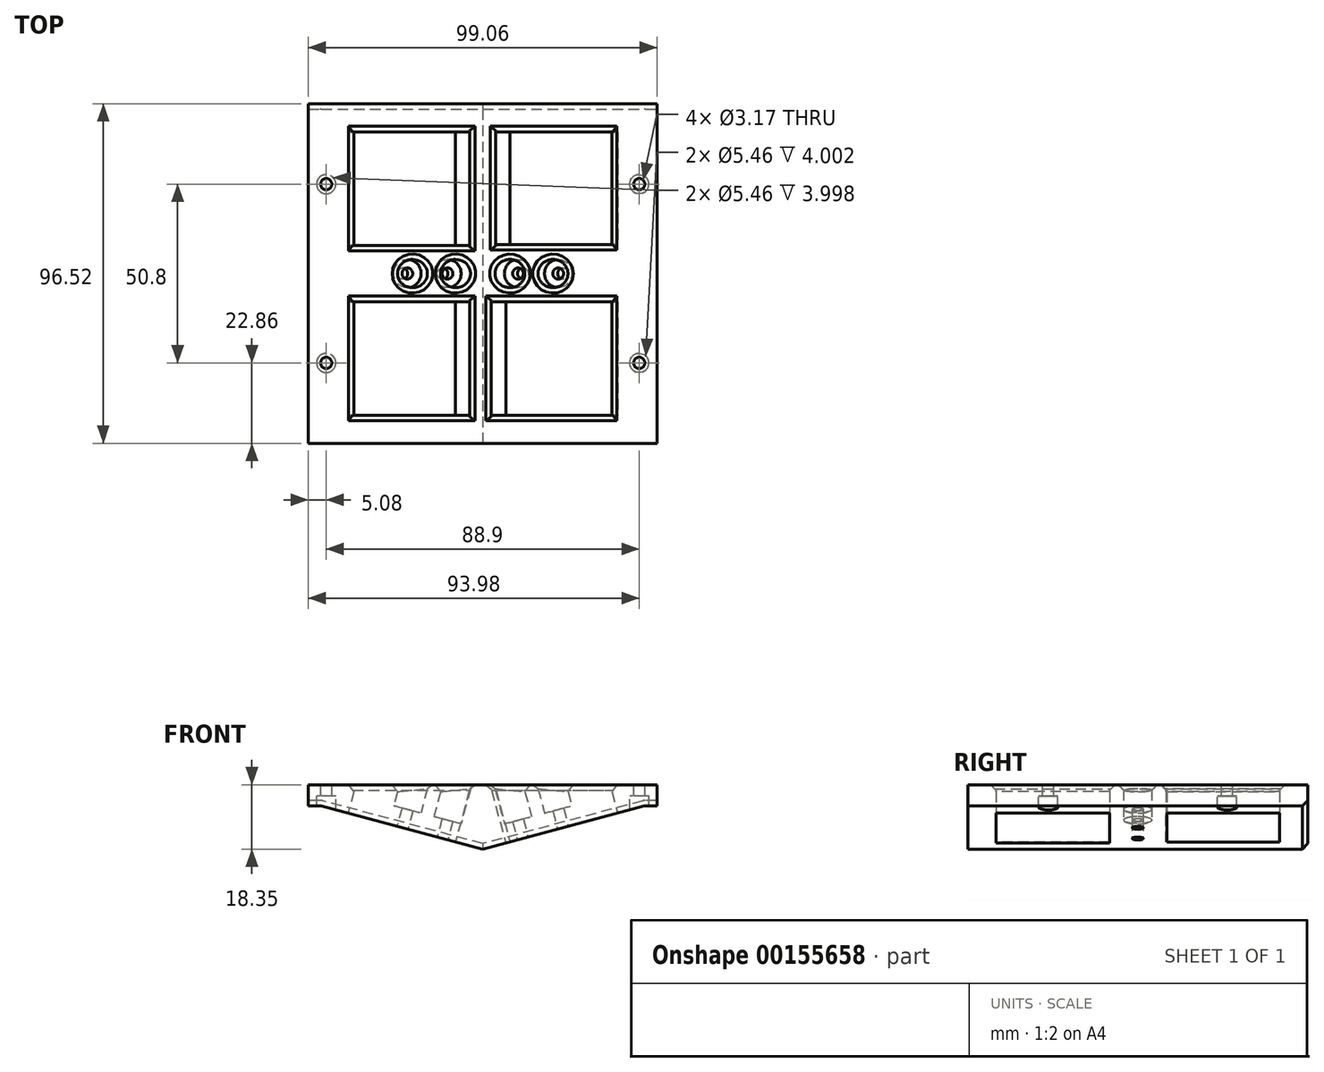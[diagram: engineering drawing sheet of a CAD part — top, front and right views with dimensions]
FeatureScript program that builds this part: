
annotation { "Feature Type Name" : "Feature", "Feature Type Description" : "" }
export const myFeature = defineFeature(function(context is Context, id is Id, definition is map)
    precondition{}
    {
        {
            var Q0;
            Q0=qCreatedBy(makeId("Top.planeOp"),FACE);
            var sketch = newSketch(context, id + "F0", { "sketchPlane" : qUnion([Q0])});
            skLineSegment(sketch, "E0", {"start": v(0, 0) * mm, "end": v(0, 48.26) * mm});
            skLineSegment(sketch, "E1", {"start": v(0, 48.26) * mm, "end": v(-49.53, 48.26) * mm});
            skLineSegment(sketch, "E2", {"start": v(-49.53, 48.26) * mm, "end": v(-49.53, 0) * mm});
            skLineSegment(sketch, "E3", {"start": v(-49.53, 0) * mm, "end": v(0, 0) * mm});
            skLineSegment(sketch, "E4", {"start": v(-49.53, 0) * mm, "end": v(-49.53, -48.26) * mm});
            skLineSegment(sketch, "E5", {"start": v(-49.53, -48.26) * mm, "end": v(0, -48.26) * mm});
            skLineSegment(sketch, "E6", {"start": v(0, -48.26) * mm, "end": v(0, 0) * mm});
            skLineSegment(sketch, "E7.MirrorCS", {"start": v(0, 48.26) * mm, "end": v(49.53, 48.26) * mm});
            skLineSegment(sketch, "E8.MirrorCS", {"start": v(49.53, 48.26) * mm, "end": v(49.53, 0) * mm});
            skLineSegment(sketch, "E9.MirrorCS", {"start": v(49.53, 0) * mm, "end": v(0, 0) * mm});
            skLineSegment(sketch, "E10.MirrorCS", {"start": v(49.53, -48.26) * mm, "end": v(0, -48.26) * mm});
            skLineSegment(sketch, "E11.MirrorCS", {"start": v(49.53, 0) * mm, "end": v(49.53, -48.26) * mm});
            skSolve(sketch);
        }
        {
            var Q0;
            Q0 = qSketchRegion(id + "F0", true);
            extrude(context, id + "F1", {"entities" : qUnion([Q0]), "depth" : 18.35 * mm});
        }
        {
            var Q0;
            Q0=makeQuery(id+"F1.opExtrude","SWEPT_FACE",FACE,{"disambiguationData":[OSD([sQuery(id+"F0.wireOp",EDGE,"E5"),sQuery(id+"F0.wireOp",EDGE,"E10.MirrorCS")])]});
            var sketch = newSketch(context, id + "F2", { "sketchPlane" : qUnion([Q0])});
            skLineSegment(sketch, "E12", {"start": v(0, 0) * mm, "end": v(-46, 12.33) * mm});
            skLineSegment(sketch, "E13", {"start": v(-46, 12.33) * mm, "end": v(-49.53, 12.33) * mm});
            skLineSegment(sketch, "E14", {"start": v(-49.53, 12.33) * mm, "end": v(-49.53, 0) * mm});
            skLineSegment(sketch, "E15", {"start": v(-49.53, 0) * mm, "end": v(0, 0) * mm});
            skLineSegment(sketch, "E16.MirrorCS", {"start": v(0, 0) * mm, "end": v(46, 12.33) * mm});
            skLineSegment(sketch, "E17.MirrorCS", {"start": v(49.53, 12.33) * mm, "end": v(49.53, 0) * mm});
            skLineSegment(sketch, "E18.MirrorCS", {"start": v(49.53, 0) * mm, "end": v(0, 0) * mm});
            skLineSegment(sketch, "E19.MirrorCS", {"start": v(46, 12.33) * mm, "end": v(49.53, 12.33) * mm});
            skSolve(sketch);
        }
        {
            var Q0;
            Q0 = qSketchRegion(id + "F2", true);
            extrude(context, id + "F3", {"entities" : qUnion([Q0]), "operationType" : NewBodyOperationType.REMOVE, "oppositeDirection" : true, "depth" : 101.6 * mm});
        }
        {
            var Q0;
            Q0=makeQuery(id+"F3.boolean.opBoolean","COPY",FACE,{"derivedFrom":makeQuery(id+"F3.opExtrude","SWEPT_FACE",FACE,{"disambiguationData":[OSD([sQuery(id+"F2.wireOp",EDGE,"E12")])]})});
            var sketch = newSketch(context, id + "F4", { "sketchPlane" : qUnion([Q0])});
            skCircle(sketch, "E20", {"center": v(-23.62, 0) * mm, "radius": 4 * mm});
            skCircle(sketch, "E21", {"center": v(-11.81, 0) * mm, "radius": 4 * mm});
            skLineSegment(sketch, "E22", {"start": v(-39.62, 40.26) * mm, "end": v(-39.62, 8) * mm});
            skLineSegment(sketch, "E23", {"start": v(-39.62, 8) * mm, "end": v(-8, 8) * mm});
            skLineSegment(sketch, "E24", {"start": v(-8, 8) * mm, "end": v(-8, 40.26) * mm});
            skLineSegment(sketch, "E25", {"start": v(-8, 40.26) * mm, "end": v(-39.62, 40.26) * mm});
            skLineSegment(sketch, "E26", {"start": v(-39.62, -8) * mm, "end": v(-39.62, -40.26) * mm});
            skLineSegment(sketch, "E27", {"start": v(-39.62, -40.26) * mm, "end": v(-8, -40.26) * mm});
            skLineSegment(sketch, "E28", {"start": v(-8, -40.26) * mm, "end": v(-8, -8) * mm});
            skLineSegment(sketch, "E29", {"start": v(-8, -8) * mm, "end": v(-39.62, -8) * mm});
            skSolve(sketch);
        }
        {
            var Q0;
            Q0 = qSketchRegion(id + "F4", true);
            extrude(context, id + "F5", {"entities" : qUnion([Q0]), "operationType" : NewBodyOperationType.REMOVE, "oppositeDirection" : true, "depth" : 25.4 * mm});
        }
        {
            var Q0;
            Q0=makeQuery(id+"F3.boolean.opBoolean","COPY",FACE,{"derivedFrom":makeQuery(id+"F3.opExtrude","SWEPT_FACE",FACE,{"disambiguationData":[OSD([sQuery(id+"F2.wireOp",EDGE,"E16.MirrorCS")])]})});
            var sketch = newSketch(context, id + "F6", { "sketchPlane" : qUnion([Q0])});
            skCircle(sketch, "E30", {"center": v(23.62, 0) * mm, "radius": 4 * mm});
            skCircle(sketch, "E31", {"center": v(11.81, 0) * mm, "radius": 4 * mm});
            skLineSegment(sketch, "E32", {"start": v(6.77, 40.26) * mm, "end": v(6.77, 8) * mm});
            skLineSegment(sketch, "E33", {"start": v(6.77, 8) * mm, "end": v(39.62, 8) * mm});
            skLineSegment(sketch, "E34", {"start": v(39.62, 8) * mm, "end": v(39.62, 40.26) * mm});
            skLineSegment(sketch, "E35", {"start": v(39.62, 40.26) * mm, "end": v(6.77, 40.26) * mm});
            skLineSegment(sketch, "E36", {"start": v(8, -8.25) * mm, "end": v(8, -40.26) * mm});
            skLineSegment(sketch, "E37", {"start": v(8, -40.26) * mm, "end": v(39.62, -40.26) * mm});
            skLineSegment(sketch, "E38", {"start": v(39.62, -40.26) * mm, "end": v(39.62, -8.25) * mm});
            skLineSegment(sketch, "E39", {"start": v(39.62, -8.25) * mm, "end": v(8, -8.25) * mm});
            skSolve(sketch);
        }
        {
            var Q0;
            Q0 = qSketchRegion(id + "F6", true);
            extrude(context, id + "F7", {"entities" : qUnion([Q0]), "operationType" : NewBodyOperationType.REMOVE, "oppositeDirection" : true, "depth" : 25.4 * mm});
        }
        {
            var Q0;
            Q0=makeQuery(id+"F3.boolean.opBoolean","COPY",FACE,{"derivedFrom":makeQuery(id+"F3.opExtrude","SWEPT_FACE",FACE,{"disambiguationData":[OSD([sQuery(id+"F2.wireOp",EDGE,"E12")])]})});
            var sketch = newSketch(context, id + "F8", { "sketchPlane" : qUnion([Q0])});
            skCircle(sketch, "E40", {"center": v(-23.62, 0) * mm, "radius": 4 * mm});
            skCircle(sketch, "E41", {"center": v(-11.81, 0) * mm, "radius": 4 * mm});
            skSolve(sketch);
        }
        {
            var Q0;
            Q0 = qSketchRegion(id + "F8", true);
            extrude(context, id + "F9", {"entities" : qUnion([Q0]), "operationType" : NewBodyOperationType.ADD, "oppositeDirection" : true, "depth" : 5.46 * mm});
        }
        {
            var Q0;
            Q0=makeQuery(id+"F9.boolean.opBoolean","MERGE",FACE,{"derivedFrom":[makeQuery(id+"F3.boolean.opBoolean","COPY",FACE,{"derivedFrom":makeQuery(id+"F3.opExtrude","SWEPT_FACE",FACE,{"disambiguationData":[OSD([sQuery(id+"F2.wireOp",EDGE,"E12")])]})}),makeQuery(id+"F9.opExtrude","CAP_FACE",FACE,{"disambiguationData":[OSD([sQuery(id+"F8.wireOp",EDGE,"pQ3E8yyw-vJVo-3WWa-J51h-BuG9gktovIe7")])],"isStart":true}),makeQuery(id+"F9.opExtrude","CAP_FACE",FACE,{"disambiguationData":[OSD([sQuery(id+"F8.wireOp",EDGE,"E40")])],"isStart":true}),makeQuery(id+"F9.opExtrude","CAP_FACE",FACE,{"disambiguationData":[OSD([sQuery(id+"F8.wireOp",EDGE,"E41")])],"isStart":true})]});
            var sketch = newSketch(context, id + "F10", { "sketchPlane" : qUnion([Q0])});
            skCircle(sketch, "E42", {"center": v(-11.81, 0) * mm, "radius": 1.59 * mm});
            skCircle(sketch, "E43", {"center": v(-23.62, 0) * mm, "radius": 1.59 * mm});
            skSolve(sketch);
        }
        {
            var Q0;
            Q0 = qSketchRegion(id + "F10", true);
            extrude(context, id + "F11", {"entities" : qUnion([Q0]), "operationType" : NewBodyOperationType.REMOVE, "oppositeDirection" : true, "depth" : 25.4 * mm});
        }
        {
            var Q0;
            Q0=makeQuery(id+"F3.boolean.opBoolean","COPY",FACE,{"derivedFrom":makeQuery(id+"F3.opExtrude","SWEPT_FACE",FACE,{"disambiguationData":[OSD([sQuery(id+"F2.wireOp",EDGE,"E16.MirrorCS")])]})});
            var sketch = newSketch(context, id + "F12", { "sketchPlane" : qUnion([Q0])});
            skCircle(sketch, "E44", {"center": v(11.81, 0) * mm, "radius": 4 * mm});
            skCircle(sketch, "E45", {"center": v(23.62, 0) * mm, "radius": 4 * mm});
            skSolve(sketch);
        }
        {
            var Q0;
            Q0 = qSketchRegion(id + "F12", true);
            extrude(context, id + "F13", {"entities" : qUnion([Q0]), "operationType" : NewBodyOperationType.ADD, "oppositeDirection" : true, "depth" : 5.4 * mm});
        }
        {
            var Q0;
            Q0=makeQuery(id+"F13.boolean.opBoolean","MERGE",FACE,{"derivedFrom":[makeQuery(id+"F3.boolean.opBoolean","COPY",FACE,{"derivedFrom":makeQuery(id+"F3.opExtrude","SWEPT_FACE",FACE,{"disambiguationData":[OSD([sQuery(id+"F2.wireOp",EDGE,"E16.MirrorCS")])]})}),makeQuery(id+"F13.opExtrude","CAP_FACE",FACE,{"disambiguationData":[OSD([sQuery(id+"F12.wireOp",EDGE,"E44")])],"isStart":true}),makeQuery(id+"F13.opExtrude","CAP_FACE",FACE,{"disambiguationData":[OSD([sQuery(id+"F12.wireOp",EDGE,"E45")])],"isStart":true})]});
            var sketch = newSketch(context, id + "F14", { "sketchPlane" : qUnion([Q0])});
            skCircle(sketch, "E46", {"center": v(11.81, 0) * mm, "radius": 1.59 * mm});
            skCircle(sketch, "E47", {"center": v(23.62, 0) * mm, "radius": 1.59 * mm});
            skSolve(sketch);
        }
        {
            var Q0;
            Q0 = qSketchRegion(id + "F14", true);
            extrude(context, id + "F15", {"entities" : qUnion([Q0]), "operationType" : NewBodyOperationType.REMOVE, "oppositeDirection" : true, "depth" : 19.05 * mm});
        }
        {
            var Q0;
            Q0=makeQuery(id+"F3.boolean.opBoolean","COPY",EDGE,{"derivedFrom":makeQuery(id+"F3.opExtrude","SWEPT_EDGE",EDGE,{"disambiguationData":[OSD([sQuery(id+"F2.wireOp",EDGE,"E12"),sQuery(id+"F2.wireOp",EDGE,"E13")])]})});
            var Q1;
            Q1=makeQuery(id+"F3.boolean.opBoolean","COPY",EDGE,{"derivedFrom":makeQuery(id+"F3.opExtrude","SWEPT_EDGE",EDGE,{"disambiguationData":[OSD([sQuery(id+"F2.wireOp",EDGE,"E16.MirrorCS"),sQuery(id+"F2.wireOp",EDGE,"E19.MirrorCS")])]})});
            fillet(context, id + "F16", {"entities" : qUnion([Q0, Q1]), "radius" : 1.59 * mm, "tangentPropagation" : true, "allowEdgeOverflow" : false});
        }
        {
            var Q0;
            Q0=makeQuery(id+"F7.boolean.opBoolean","INTERSECT",EDGE,{"derivedFrom":[makeQuery(id+"F1.opExtrude","CAP_FACE",FACE,{"disambiguationData":[OSD([sQuery(id+"F0.wireOp",EDGE,"E1"),sQuery(id+"F0.wireOp",EDGE,"E2"),sQuery(id+"F0.wireOp",EDGE,"E4"),sQuery(id+"F0.wireOp",EDGE,"E5"),sQuery(id+"F0.wireOp",EDGE,"E7.MirrorCS"),sQuery(id+"F0.wireOp",EDGE,"E8.MirrorCS"),sQuery(id+"F0.wireOp",EDGE,"E10.MirrorCS"),sQuery(id+"F0.wireOp",EDGE,"E11.MirrorCS")])],"isStart":false}),makeQuery(id+"F7.opExtrude","SWEPT_FACE",FACE,{"disambiguationData":[OSD([sQuery(id+"F6.wireOp",EDGE,"E31")])]})]});
            var Q1;
            Q1=makeQuery(id+"F7.boolean.opBoolean","INTERSECT",EDGE,{"derivedFrom":[makeQuery(id+"F1.opExtrude","CAP_FACE",FACE,{"disambiguationData":[OSD([sQuery(id+"F0.wireOp",EDGE,"E1"),sQuery(id+"F0.wireOp",EDGE,"E2"),sQuery(id+"F0.wireOp",EDGE,"E4"),sQuery(id+"F0.wireOp",EDGE,"E5"),sQuery(id+"F0.wireOp",EDGE,"E7.MirrorCS"),sQuery(id+"F0.wireOp",EDGE,"E8.MirrorCS"),sQuery(id+"F0.wireOp",EDGE,"E10.MirrorCS"),sQuery(id+"F0.wireOp",EDGE,"E11.MirrorCS")])],"isStart":false}),makeQuery(id+"F7.opExtrude","SWEPT_FACE",FACE,{"disambiguationData":[OSD([sQuery(id+"F6.wireOp",EDGE,"E30")])]})]});
            var Q2;
            Q2=makeQuery(id+"F5.boolean.opBoolean","INTERSECT",EDGE,{"derivedFrom":[makeQuery(id+"F1.opExtrude","CAP_FACE",FACE,{"disambiguationData":[OSD([sQuery(id+"F0.wireOp",EDGE,"E1"),sQuery(id+"F0.wireOp",EDGE,"E2"),sQuery(id+"F0.wireOp",EDGE,"E4"),sQuery(id+"F0.wireOp",EDGE,"E5"),sQuery(id+"F0.wireOp",EDGE,"E7.MirrorCS"),sQuery(id+"F0.wireOp",EDGE,"E8.MirrorCS"),sQuery(id+"F0.wireOp",EDGE,"E10.MirrorCS"),sQuery(id+"F0.wireOp",EDGE,"E11.MirrorCS")])],"isStart":false}),makeQuery(id+"F5.opExtrude","SWEPT_FACE",FACE,{"disambiguationData":[OSD([sQuery(id+"F4.wireOp",EDGE,"E21")])]})]});
            var Q3;
            Q3=makeQuery(id+"F5.boolean.opBoolean","INTERSECT",EDGE,{"derivedFrom":[makeQuery(id+"F1.opExtrude","CAP_FACE",FACE,{"disambiguationData":[OSD([sQuery(id+"F0.wireOp",EDGE,"E1"),sQuery(id+"F0.wireOp",EDGE,"E2"),sQuery(id+"F0.wireOp",EDGE,"E4"),sQuery(id+"F0.wireOp",EDGE,"E5"),sQuery(id+"F0.wireOp",EDGE,"E7.MirrorCS"),sQuery(id+"F0.wireOp",EDGE,"E8.MirrorCS"),sQuery(id+"F0.wireOp",EDGE,"E10.MirrorCS"),sQuery(id+"F0.wireOp",EDGE,"E11.MirrorCS")])],"isStart":false}),makeQuery(id+"F5.opExtrude","SWEPT_FACE",FACE,{"disambiguationData":[OSD([sQuery(id+"F4.wireOp",EDGE,"E20")])]})]});
            var Q4;
            Q4=makeQuery(id+"F5.boolean.opBoolean","INTERSECT",EDGE,{"derivedFrom":[makeQuery(id+"F1.opExtrude","CAP_FACE",FACE,{"disambiguationData":[OSD([sQuery(id+"F0.wireOp",EDGE,"E1"),sQuery(id+"F0.wireOp",EDGE,"E2"),sQuery(id+"F0.wireOp",EDGE,"E4"),sQuery(id+"F0.wireOp",EDGE,"E5"),sQuery(id+"F0.wireOp",EDGE,"E7.MirrorCS"),sQuery(id+"F0.wireOp",EDGE,"E8.MirrorCS"),sQuery(id+"F0.wireOp",EDGE,"E10.MirrorCS"),sQuery(id+"F0.wireOp",EDGE,"E11.MirrorCS")])],"isStart":false}),makeQuery(id+"F5.opExtrude","SWEPT_FACE",FACE,{"disambiguationData":[OSD([sQuery(id+"F4.wireOp",EDGE,"E23")])]})]});
            var Q5;
            Q5=makeQuery(id+"F5.boolean.opBoolean","INTERSECT",EDGE,{"derivedFrom":[makeQuery(id+"F1.opExtrude","CAP_FACE",FACE,{"disambiguationData":[OSD([sQuery(id+"F0.wireOp",EDGE,"E1"),sQuery(id+"F0.wireOp",EDGE,"E2"),sQuery(id+"F0.wireOp",EDGE,"E4"),sQuery(id+"F0.wireOp",EDGE,"E5"),sQuery(id+"F0.wireOp",EDGE,"E7.MirrorCS"),sQuery(id+"F0.wireOp",EDGE,"E8.MirrorCS"),sQuery(id+"F0.wireOp",EDGE,"E10.MirrorCS"),sQuery(id+"F0.wireOp",EDGE,"E11.MirrorCS")])],"isStart":false}),makeQuery(id+"F5.opExtrude","SWEPT_FACE",FACE,{"disambiguationData":[OSD([sQuery(id+"F4.wireOp",EDGE,"E22")])]})]});
            var Q6;
            Q6=makeQuery(id+"F5.boolean.opBoolean","INTERSECT",EDGE,{"derivedFrom":[makeQuery(id+"F1.opExtrude","CAP_FACE",FACE,{"disambiguationData":[OSD([sQuery(id+"F0.wireOp",EDGE,"E1"),sQuery(id+"F0.wireOp",EDGE,"E2"),sQuery(id+"F0.wireOp",EDGE,"E4"),sQuery(id+"F0.wireOp",EDGE,"E5"),sQuery(id+"F0.wireOp",EDGE,"E7.MirrorCS"),sQuery(id+"F0.wireOp",EDGE,"E8.MirrorCS"),sQuery(id+"F0.wireOp",EDGE,"E10.MirrorCS"),sQuery(id+"F0.wireOp",EDGE,"E11.MirrorCS")])],"isStart":false}),makeQuery(id+"F5.opExtrude","SWEPT_FACE",FACE,{"disambiguationData":[OSD([sQuery(id+"F4.wireOp",EDGE,"E25")])]})]});
            var Q7;
            Q7=makeQuery(id+"F5.boolean.opBoolean","INTERSECT",EDGE,{"derivedFrom":[makeQuery(id+"F1.opExtrude","CAP_FACE",FACE,{"disambiguationData":[OSD([sQuery(id+"F0.wireOp",EDGE,"E1"),sQuery(id+"F0.wireOp",EDGE,"E2"),sQuery(id+"F0.wireOp",EDGE,"E4"),sQuery(id+"F0.wireOp",EDGE,"E5"),sQuery(id+"F0.wireOp",EDGE,"E7.MirrorCS"),sQuery(id+"F0.wireOp",EDGE,"E8.MirrorCS"),sQuery(id+"F0.wireOp",EDGE,"E10.MirrorCS"),sQuery(id+"F0.wireOp",EDGE,"E11.MirrorCS")])],"isStart":false}),makeQuery(id+"F5.opExtrude","SWEPT_FACE",FACE,{"disambiguationData":[OSD([sQuery(id+"F4.wireOp",EDGE,"E24")])]})]});
            var Q8;
            Q8=makeQuery(id+"F7.boolean.opBoolean","INTERSECT",EDGE,{"derivedFrom":[makeQuery(id+"F1.opExtrude","CAP_FACE",FACE,{"disambiguationData":[OSD([sQuery(id+"F0.wireOp",EDGE,"E1"),sQuery(id+"F0.wireOp",EDGE,"E2"),sQuery(id+"F0.wireOp",EDGE,"E4"),sQuery(id+"F0.wireOp",EDGE,"E5"),sQuery(id+"F0.wireOp",EDGE,"E7.MirrorCS"),sQuery(id+"F0.wireOp",EDGE,"E8.MirrorCS"),sQuery(id+"F0.wireOp",EDGE,"E10.MirrorCS"),sQuery(id+"F0.wireOp",EDGE,"E11.MirrorCS")])],"isStart":false}),makeQuery(id+"F7.opExtrude","SWEPT_FACE",FACE,{"disambiguationData":[OSD([sQuery(id+"F6.wireOp",EDGE,"E35")])]})]});
            var Q9;
            Q9=makeQuery(id+"F7.boolean.opBoolean","INTERSECT",EDGE,{"derivedFrom":[makeQuery(id+"F1.opExtrude","CAP_FACE",FACE,{"disambiguationData":[OSD([sQuery(id+"F0.wireOp",EDGE,"E1"),sQuery(id+"F0.wireOp",EDGE,"E2"),sQuery(id+"F0.wireOp",EDGE,"E4"),sQuery(id+"F0.wireOp",EDGE,"E5"),sQuery(id+"F0.wireOp",EDGE,"E7.MirrorCS"),sQuery(id+"F0.wireOp",EDGE,"E8.MirrorCS"),sQuery(id+"F0.wireOp",EDGE,"E10.MirrorCS"),sQuery(id+"F0.wireOp",EDGE,"E11.MirrorCS")])],"isStart":false}),makeQuery(id+"F7.opExtrude","SWEPT_FACE",FACE,{"disambiguationData":[OSD([sQuery(id+"F6.wireOp",EDGE,"E32")])]})]});
            var Q10;
            Q10=makeQuery(id+"F7.boolean.opBoolean","INTERSECT",EDGE,{"derivedFrom":[makeQuery(id+"F1.opExtrude","CAP_FACE",FACE,{"disambiguationData":[OSD([sQuery(id+"F0.wireOp",EDGE,"E1"),sQuery(id+"F0.wireOp",EDGE,"E2"),sQuery(id+"F0.wireOp",EDGE,"E4"),sQuery(id+"F0.wireOp",EDGE,"E5"),sQuery(id+"F0.wireOp",EDGE,"E7.MirrorCS"),sQuery(id+"F0.wireOp",EDGE,"E8.MirrorCS"),sQuery(id+"F0.wireOp",EDGE,"E10.MirrorCS"),sQuery(id+"F0.wireOp",EDGE,"E11.MirrorCS")])],"isStart":false}),makeQuery(id+"F7.opExtrude","SWEPT_FACE",FACE,{"disambiguationData":[OSD([sQuery(id+"F6.wireOp",EDGE,"E33")])]})]});
            var Q11;
            Q11=makeQuery(id+"F7.boolean.opBoolean","INTERSECT",EDGE,{"derivedFrom":[makeQuery(id+"F1.opExtrude","CAP_FACE",FACE,{"disambiguationData":[OSD([sQuery(id+"F0.wireOp",EDGE,"E1"),sQuery(id+"F0.wireOp",EDGE,"E2"),sQuery(id+"F0.wireOp",EDGE,"E4"),sQuery(id+"F0.wireOp",EDGE,"E5"),sQuery(id+"F0.wireOp",EDGE,"E7.MirrorCS"),sQuery(id+"F0.wireOp",EDGE,"E8.MirrorCS"),sQuery(id+"F0.wireOp",EDGE,"E10.MirrorCS"),sQuery(id+"F0.wireOp",EDGE,"E11.MirrorCS")])],"isStart":false}),makeQuery(id+"F7.opExtrude","SWEPT_FACE",FACE,{"disambiguationData":[OSD([sQuery(id+"F6.wireOp",EDGE,"E34")])]})]});
            var Q12;
            Q12=makeQuery(id+"F7.boolean.opBoolean","INTERSECT",EDGE,{"derivedFrom":[makeQuery(id+"F1.opExtrude","CAP_FACE",FACE,{"disambiguationData":[OSD([sQuery(id+"F0.wireOp",EDGE,"E1"),sQuery(id+"F0.wireOp",EDGE,"E2"),sQuery(id+"F0.wireOp",EDGE,"E4"),sQuery(id+"F0.wireOp",EDGE,"E5"),sQuery(id+"F0.wireOp",EDGE,"E7.MirrorCS"),sQuery(id+"F0.wireOp",EDGE,"E8.MirrorCS"),sQuery(id+"F0.wireOp",EDGE,"E10.MirrorCS"),sQuery(id+"F0.wireOp",EDGE,"E11.MirrorCS")])],"isStart":false}),makeQuery(id+"F7.opExtrude","SWEPT_FACE",FACE,{"disambiguationData":[OSD([sQuery(id+"F6.wireOp",EDGE,"E39")])]})]});
            var Q13;
            Q13=makeQuery(id+"F7.boolean.opBoolean","INTERSECT",EDGE,{"derivedFrom":[makeQuery(id+"F1.opExtrude","CAP_FACE",FACE,{"disambiguationData":[OSD([sQuery(id+"F0.wireOp",EDGE,"E1"),sQuery(id+"F0.wireOp",EDGE,"E2"),sQuery(id+"F0.wireOp",EDGE,"E4"),sQuery(id+"F0.wireOp",EDGE,"E5"),sQuery(id+"F0.wireOp",EDGE,"E7.MirrorCS"),sQuery(id+"F0.wireOp",EDGE,"E8.MirrorCS"),sQuery(id+"F0.wireOp",EDGE,"E10.MirrorCS"),sQuery(id+"F0.wireOp",EDGE,"E11.MirrorCS")])],"isStart":false}),makeQuery(id+"F7.opExtrude","SWEPT_FACE",FACE,{"disambiguationData":[OSD([sQuery(id+"F6.wireOp",EDGE,"E38")])]})]});
            var Q14;
            Q14=makeQuery(id+"F7.boolean.opBoolean","INTERSECT",EDGE,{"derivedFrom":[makeQuery(id+"F1.opExtrude","CAP_FACE",FACE,{"disambiguationData":[OSD([sQuery(id+"F0.wireOp",EDGE,"E1"),sQuery(id+"F0.wireOp",EDGE,"E2"),sQuery(id+"F0.wireOp",EDGE,"E4"),sQuery(id+"F0.wireOp",EDGE,"E5"),sQuery(id+"F0.wireOp",EDGE,"E7.MirrorCS"),sQuery(id+"F0.wireOp",EDGE,"E8.MirrorCS"),sQuery(id+"F0.wireOp",EDGE,"E10.MirrorCS"),sQuery(id+"F0.wireOp",EDGE,"E11.MirrorCS")])],"isStart":false}),makeQuery(id+"F7.opExtrude","SWEPT_FACE",FACE,{"disambiguationData":[OSD([sQuery(id+"F6.wireOp",EDGE,"E37")])]})]});
            var Q15;
            Q15=makeQuery(id+"F7.boolean.opBoolean","INTERSECT",EDGE,{"derivedFrom":[makeQuery(id+"F1.opExtrude","CAP_FACE",FACE,{"disambiguationData":[OSD([sQuery(id+"F0.wireOp",EDGE,"E1"),sQuery(id+"F0.wireOp",EDGE,"E2"),sQuery(id+"F0.wireOp",EDGE,"E4"),sQuery(id+"F0.wireOp",EDGE,"E5"),sQuery(id+"F0.wireOp",EDGE,"E7.MirrorCS"),sQuery(id+"F0.wireOp",EDGE,"E8.MirrorCS"),sQuery(id+"F0.wireOp",EDGE,"E10.MirrorCS"),sQuery(id+"F0.wireOp",EDGE,"E11.MirrorCS")])],"isStart":false}),makeQuery(id+"F7.opExtrude","SWEPT_FACE",FACE,{"disambiguationData":[OSD([sQuery(id+"F6.wireOp",EDGE,"E36")])]})]});
            var Q16;
            Q16=makeQuery(id+"F5.boolean.opBoolean","INTERSECT",EDGE,{"derivedFrom":[makeQuery(id+"F1.opExtrude","CAP_FACE",FACE,{"disambiguationData":[OSD([sQuery(id+"F0.wireOp",EDGE,"E1"),sQuery(id+"F0.wireOp",EDGE,"E2"),sQuery(id+"F0.wireOp",EDGE,"E4"),sQuery(id+"F0.wireOp",EDGE,"E5"),sQuery(id+"F0.wireOp",EDGE,"E7.MirrorCS"),sQuery(id+"F0.wireOp",EDGE,"E8.MirrorCS"),sQuery(id+"F0.wireOp",EDGE,"E10.MirrorCS"),sQuery(id+"F0.wireOp",EDGE,"E11.MirrorCS")])],"isStart":false}),makeQuery(id+"F5.opExtrude","SWEPT_FACE",FACE,{"disambiguationData":[OSD([sQuery(id+"F4.wireOp",EDGE,"E28")])]})]});
            var Q17;
            Q17=makeQuery(id+"F5.boolean.opBoolean","INTERSECT",EDGE,{"derivedFrom":[makeQuery(id+"F1.opExtrude","CAP_FACE",FACE,{"disambiguationData":[OSD([sQuery(id+"F0.wireOp",EDGE,"E1"),sQuery(id+"F0.wireOp",EDGE,"E2"),sQuery(id+"F0.wireOp",EDGE,"E4"),sQuery(id+"F0.wireOp",EDGE,"E5"),sQuery(id+"F0.wireOp",EDGE,"E7.MirrorCS"),sQuery(id+"F0.wireOp",EDGE,"E8.MirrorCS"),sQuery(id+"F0.wireOp",EDGE,"E10.MirrorCS"),sQuery(id+"F0.wireOp",EDGE,"E11.MirrorCS")])],"isStart":false}),makeQuery(id+"F5.opExtrude","SWEPT_FACE",FACE,{"disambiguationData":[OSD([sQuery(id+"F4.wireOp",EDGE,"E27")])]})]});
            var Q18;
            Q18=makeQuery(id+"F5.boolean.opBoolean","INTERSECT",EDGE,{"derivedFrom":[makeQuery(id+"F1.opExtrude","CAP_FACE",FACE,{"disambiguationData":[OSD([sQuery(id+"F0.wireOp",EDGE,"E1"),sQuery(id+"F0.wireOp",EDGE,"E2"),sQuery(id+"F0.wireOp",EDGE,"E4"),sQuery(id+"F0.wireOp",EDGE,"E5"),sQuery(id+"F0.wireOp",EDGE,"E7.MirrorCS"),sQuery(id+"F0.wireOp",EDGE,"E8.MirrorCS"),sQuery(id+"F0.wireOp",EDGE,"E10.MirrorCS"),sQuery(id+"F0.wireOp",EDGE,"E11.MirrorCS")])],"isStart":false}),makeQuery(id+"F5.opExtrude","SWEPT_FACE",FACE,{"disambiguationData":[OSD([sQuery(id+"F4.wireOp",EDGE,"E26")])]})]});
            var Q19;
            Q19=makeQuery(id+"F5.boolean.opBoolean","INTERSECT",EDGE,{"derivedFrom":[makeQuery(id+"F1.opExtrude","CAP_FACE",FACE,{"disambiguationData":[OSD([sQuery(id+"F0.wireOp",EDGE,"E1"),sQuery(id+"F0.wireOp",EDGE,"E2"),sQuery(id+"F0.wireOp",EDGE,"E4"),sQuery(id+"F0.wireOp",EDGE,"E5"),sQuery(id+"F0.wireOp",EDGE,"E7.MirrorCS"),sQuery(id+"F0.wireOp",EDGE,"E8.MirrorCS"),sQuery(id+"F0.wireOp",EDGE,"E10.MirrorCS"),sQuery(id+"F0.wireOp",EDGE,"E11.MirrorCS")])],"isStart":false}),makeQuery(id+"F5.opExtrude","SWEPT_FACE",FACE,{"disambiguationData":[OSD([sQuery(id+"F4.wireOp",EDGE,"E29")])]})]});
            var Q20;
            Q20=makeQuery(id+"FYnI5kBaEs5TiWY_1.boolean.opBoolean","INTERSECT",EDGE,{"derivedFrom":[makeQuery(id+"F1.opExtrude","CAP_FACE",FACE,{"disambiguationData":[OSD([sQuery(id+"F0.wireOp",EDGE,"E1"),sQuery(id+"F0.wireOp",EDGE,"E2"),sQuery(id+"F0.wireOp",EDGE,"E4"),sQuery(id+"F0.wireOp",EDGE,"E5"),sQuery(id+"F0.wireOp",EDGE,"E7.MirrorCS"),sQuery(id+"F0.wireOp",EDGE,"E8.MirrorCS"),sQuery(id+"F0.wireOp",EDGE,"E10.MirrorCS"),sQuery(id+"F0.wireOp",EDGE,"E11.MirrorCS")])],"isStart":false}),makeQuery(id+"FYnI5kBaEs5TiWY_1.opExtrude","SWEPT_FACE",FACE,{"disambiguationData":[OSD([sQuery(id+"FR68opKNNehgeix_1.wireOp",EDGE,"sBlfLD54-xqRK-Qegp-v1L6-Wi3MA03pmQhw")])]})]});
            var Q21;
            Q21=makeQuery(id+"FYnI5kBaEs5TiWY_1.boolean.opBoolean","INTERSECT",EDGE,{"derivedFrom":[makeQuery(id+"F1.opExtrude","CAP_FACE",FACE,{"disambiguationData":[OSD([sQuery(id+"F0.wireOp",EDGE,"E1"),sQuery(id+"F0.wireOp",EDGE,"E2"),sQuery(id+"F0.wireOp",EDGE,"E4"),sQuery(id+"F0.wireOp",EDGE,"E5"),sQuery(id+"F0.wireOp",EDGE,"E7.MirrorCS"),sQuery(id+"F0.wireOp",EDGE,"E8.MirrorCS"),sQuery(id+"F0.wireOp",EDGE,"E10.MirrorCS"),sQuery(id+"F0.wireOp",EDGE,"E11.MirrorCS")])],"isStart":false}),makeQuery(id+"FYnI5kBaEs5TiWY_1.opExtrude","SWEPT_FACE",FACE,{"disambiguationData":[OSD([sQuery(id+"FR68opKNNehgeix_1.wireOp",EDGE,"66f9165e-bbf7-40d7-9a60-d5be4ddf76150.MirrorC")])]})]});
            var Q22;
            Q22=makeQuery(id+"FYnI5kBaEs5TiWY_1.boolean.opBoolean","INTERSECT",EDGE,{"derivedFrom":[makeQuery(id+"F1.opExtrude","CAP_FACE",FACE,{"disambiguationData":[OSD([sQuery(id+"F0.wireOp",EDGE,"E1"),sQuery(id+"F0.wireOp",EDGE,"E2"),sQuery(id+"F0.wireOp",EDGE,"E4"),sQuery(id+"F0.wireOp",EDGE,"E5"),sQuery(id+"F0.wireOp",EDGE,"E7.MirrorCS"),sQuery(id+"F0.wireOp",EDGE,"E8.MirrorCS"),sQuery(id+"F0.wireOp",EDGE,"E10.MirrorCS"),sQuery(id+"F0.wireOp",EDGE,"E11.MirrorCS")])],"isStart":false}),makeQuery(id+"FYnI5kBaEs5TiWY_1.opExtrude","SWEPT_FACE",FACE,{"disambiguationData":[OSD([sQuery(id+"FR68opKNNehgeix_1.wireOp",EDGE,"DjPKJ1o5-8hDy-dqke-Bfdb-okCK0ouIeChg")])]})]});
            var Q23;
            Q23=makeQuery(id+"FYnI5kBaEs5TiWY_1.boolean.opBoolean","INTERSECT",EDGE,{"derivedFrom":[makeQuery(id+"F1.opExtrude","CAP_FACE",FACE,{"disambiguationData":[OSD([sQuery(id+"F0.wireOp",EDGE,"E1"),sQuery(id+"F0.wireOp",EDGE,"E2"),sQuery(id+"F0.wireOp",EDGE,"E4"),sQuery(id+"F0.wireOp",EDGE,"E5"),sQuery(id+"F0.wireOp",EDGE,"E7.MirrorCS"),sQuery(id+"F0.wireOp",EDGE,"E8.MirrorCS"),sQuery(id+"F0.wireOp",EDGE,"E10.MirrorCS"),sQuery(id+"F0.wireOp",EDGE,"E11.MirrorCS")])],"isStart":false}),makeQuery(id+"FYnI5kBaEs5TiWY_1.opExtrude","SWEPT_FACE",FACE,{"disambiguationData":[OSD([sQuery(id+"FR68opKNNehgeix_1.wireOp",EDGE,"abb4d433-8925-459a-8b4c-c09df92401800.MirrorC")])]})]});
            var Q24;
            Q24=makeQuery(id+"FYnI5kBaEs5TiWY_1.boolean.opBoolean","INTERSECT",EDGE,{"derivedFrom":[makeQuery(id+"F1.opExtrude","CAP_FACE",FACE,{"disambiguationData":[OSD([sQuery(id+"F0.wireOp",EDGE,"E1"),sQuery(id+"F0.wireOp",EDGE,"E2"),sQuery(id+"F0.wireOp",EDGE,"E4"),sQuery(id+"F0.wireOp",EDGE,"E5"),sQuery(id+"F0.wireOp",EDGE,"E7.MirrorCS"),sQuery(id+"F0.wireOp",EDGE,"E8.MirrorCS"),sQuery(id+"F0.wireOp",EDGE,"E10.MirrorCS"),sQuery(id+"F0.wireOp",EDGE,"E11.MirrorCS")])],"isStart":false}),makeQuery(id+"FYnI5kBaEs5TiWY_1.opExtrude","SWEPT_FACE",FACE,{"disambiguationData":[OSD([sQuery(id+"FR68opKNNehgeix_1.wireOp",EDGE,"c1fd37d2-cbfd-40f1-bfbc-11960e9b0f610.MirrorC")])]})]});
            var Q25;
            Q25=makeQuery(id+"FYnI5kBaEs5TiWY_1.boolean.opBoolean","INTERSECT",EDGE,{"derivedFrom":[makeQuery(id+"F1.opExtrude","CAP_FACE",FACE,{"disambiguationData":[OSD([sQuery(id+"F0.wireOp",EDGE,"E1"),sQuery(id+"F0.wireOp",EDGE,"E2"),sQuery(id+"F0.wireOp",EDGE,"E4"),sQuery(id+"F0.wireOp",EDGE,"E5"),sQuery(id+"F0.wireOp",EDGE,"E7.MirrorCS"),sQuery(id+"F0.wireOp",EDGE,"E8.MirrorCS"),sQuery(id+"F0.wireOp",EDGE,"E10.MirrorCS"),sQuery(id+"F0.wireOp",EDGE,"E11.MirrorCS")])],"isStart":false}),makeQuery(id+"FYnI5kBaEs5TiWY_1.opExtrude","SWEPT_FACE",FACE,{"disambiguationData":[OSD([sQuery(id+"FR68opKNNehgeix_1.wireOp",EDGE,"b0ff50b0-cbe2-48a0-8f5d-c420156ca1e70.MirrorC")])]})]});
            var Q26;
            Q26=makeQuery(id+"F3.boolean.opBoolean","INTERSECT",EDGE,{"derivedFrom":[makeQuery(id+"F1.opExtrude","SWEPT_FACE",FACE,{"disambiguationData":[OSD([sQuery(id+"F0.wireOp",EDGE,"E1"),sQuery(id+"F0.wireOp",EDGE,"E7.MirrorCS")])]}),makeQuery(id+"F3.opExtrude","SWEPT_FACE",FACE,{"disambiguationData":[OSD([sQuery(id+"F2.wireOp",EDGE,"E12")])]})]});
            var Q27;
            Q27=makeQuery(id+"F3.boolean.opBoolean","INTERSECT",EDGE,{"derivedFrom":[makeQuery(id+"F1.opExtrude","SWEPT_FACE",FACE,{"disambiguationData":[OSD([sQuery(id+"F0.wireOp",EDGE,"E1"),sQuery(id+"F0.wireOp",EDGE,"E7.MirrorCS")])]}),makeQuery(id+"F3.opExtrude","SWEPT_FACE",FACE,{"disambiguationData":[OSD([sQuery(id+"F2.wireOp",EDGE,"E13")])]})]});
            var Q28;
            Q28=makeQuery(id+"F3.boolean.opBoolean","COPY",EDGE,{"derivedFrom":makeQuery(id+"F3.opExtrude","SWEPT_EDGE",EDGE,{"disambiguationData":[OSD([sQuery(id+"F0.wireOp",EDGE,"E4"),sQuery(id+"F0.wireOp",EDGE,"E5"),sQuery(id+"F2.wireOp",EDGE,"E13"),sQuery(id+"F2.wireOp",EDGE,"E14")])]})});
            var Q29;
            Q29=makeQuery(id+"F3.boolean.opBoolean","COPY",EDGE,{"derivedFrom":makeQuery(id+"F3.opExtrude","CAP_EDGE",EDGE,{"disambiguationData":[OSD([sQuery(id+"F2.wireOp",EDGE,"E13")])],"isStart":true})});
            var Q30;
            Q30=makeQuery(id+"F3.boolean.opBoolean","COPY",EDGE,{"derivedFrom":makeQuery(id+"F3.opExtrude","CAP_EDGE",EDGE,{"disambiguationData":[OSD([sQuery(id+"F2.wireOp",EDGE,"E12")])],"isStart":true})});
            var Q31;
            Q31=makeQuery(id+"F3.boolean.opBoolean","COPY",EDGE,{"derivedFrom":makeQuery(id+"F3.opExtrude","CAP_EDGE",EDGE,{"disambiguationData":[OSD([sQuery(id+"F2.wireOp",EDGE,"E16.MirrorCS")])],"isStart":true})});
            var Q32;
            Q32=makeQuery(id+"F3.boolean.opBoolean","COPY",EDGE,{"derivedFrom":makeQuery(id+"F3.opExtrude","CAP_EDGE",EDGE,{"disambiguationData":[OSD([sQuery(id+"F2.wireOp",EDGE,"E19.MirrorCS")])],"isStart":true})});
            var Q33;
            Q33=makeQuery(id+"F3.boolean.opBoolean","COPY",EDGE,{"derivedFrom":makeQuery(id+"F3.opExtrude","SWEPT_EDGE",EDGE,{"disambiguationData":[OSD([sQuery(id+"F0.wireOp",EDGE,"E10.MirrorCS"),sQuery(id+"F0.wireOp",EDGE,"E11.MirrorCS"),sQuery(id+"F2.wireOp",EDGE,"E17.MirrorCS"),sQuery(id+"F2.wireOp",EDGE,"E19.MirrorCS")])]})});
            var Q34;
            Q34=makeQuery(id+"F3.boolean.opBoolean","INTERSECT",EDGE,{"derivedFrom":[makeQuery(id+"F1.opExtrude","SWEPT_FACE",FACE,{"disambiguationData":[OSD([sQuery(id+"F0.wireOp",EDGE,"E1"),sQuery(id+"F0.wireOp",EDGE,"E7.MirrorCS")])]}),makeQuery(id+"F3.opExtrude","SWEPT_FACE",FACE,{"disambiguationData":[OSD([sQuery(id+"F2.wireOp",EDGE,"E19.MirrorCS")])]})]});
            var Q35;
            Q35=makeQuery(id+"F3.boolean.opBoolean","INTERSECT",EDGE,{"derivedFrom":[makeQuery(id+"F1.opExtrude","SWEPT_FACE",FACE,{"disambiguationData":[OSD([sQuery(id+"F0.wireOp",EDGE,"E1"),sQuery(id+"F0.wireOp",EDGE,"E7.MirrorCS")])]}),makeQuery(id+"F3.opExtrude","SWEPT_FACE",FACE,{"disambiguationData":[OSD([sQuery(id+"F2.wireOp",EDGE,"E16.MirrorCS")])]})]});
            chamfer(context, id + "F17", {"entities" : qUnion([Q0, Q1, Q2, Q3, Q4, Q5, Q6, Q7, Q8, Q9, Q10, Q11, Q12, Q13, Q14, Q15, Q16, Q17, Q18, Q19, Q20, Q21, Q22, Q23, Q24, Q25, Q26, Q27, Q28, Q29, Q30, Q31, Q32, Q33, Q34, Q35]), "width" : 1.56 * mm, "tangentPropagation" : true});
        }
        {
            var Q0;
            Q0=makeQuery(id+"F1.opExtrude","CAP_FACE",FACE,{"disambiguationData":[OSD([sQuery(id+"F0.wireOp",EDGE,"E1"),sQuery(id+"F0.wireOp",EDGE,"E2"),sQuery(id+"F0.wireOp",EDGE,"E4"),sQuery(id+"F0.wireOp",EDGE,"E5"),sQuery(id+"F0.wireOp",EDGE,"E7.MirrorCS"),sQuery(id+"F0.wireOp",EDGE,"E8.MirrorCS"),sQuery(id+"F0.wireOp",EDGE,"E10.MirrorCS"),sQuery(id+"F0.wireOp",EDGE,"E11.MirrorCS")])],"isStart":false});
            var sketch = newSketch(context, id + "F18", { "sketchPlane" : qUnion([Q0])});
            skCircle(sketch, "E48", {"center": v(-44.45, -25.4) * mm, "radius": 2.73 * mm});
            skCircle(sketch, "E49.MirrorC", {"center": v(-44.45, 25.4) * mm, "radius": 2.73 * mm});
            skCircle(sketch, "E50.MirrorC", {"center": v(44.45, -25.4) * mm, "radius": 2.73 * mm});
            skCircle(sketch, "E51.MirrorC", {"center": v(44.45, 25.4) * mm, "radius": 2.73 * mm});
            skSolve(sketch);
        }
        {
            var Q0;
            Q0 = qSketchRegion(id + "F18", true);
            extrude(context, id + "F19", {"entities" : qUnion([Q0]), "operationType" : NewBodyOperationType.REMOVE, "endBound" : BoundingType.THROUGH_ALL, "oppositeDirection" : true, "depth" : 12.7 * mm});
        }
        {
            var Q0;
            Q0=makeQuery(id+"F1.opExtrude","CAP_FACE",FACE,{"disambiguationData":[OSD([sQuery(id+"F0.wireOp",EDGE,"E1"),sQuery(id+"F0.wireOp",EDGE,"E2"),sQuery(id+"F0.wireOp",EDGE,"E4"),sQuery(id+"F0.wireOp",EDGE,"E5"),sQuery(id+"F0.wireOp",EDGE,"E7.MirrorCS"),sQuery(id+"F0.wireOp",EDGE,"E8.MirrorCS"),sQuery(id+"F0.wireOp",EDGE,"E10.MirrorCS"),sQuery(id+"F0.wireOp",EDGE,"E11.MirrorCS")])],"isStart":false});
            var sketch = newSketch(context, id + "F20", { "sketchPlane" : qUnion([Q0])});
            skCircle(sketch, "E52", {"center": v(-44.45, -25.4) * mm, "radius": 2.73 * mm});
            skCircle(sketch, "E53.MirrorC", {"center": v(44.45, -25.4) * mm, "radius": 2.73 * mm});
            skCircle(sketch, "E54.MirrorC", {"center": v(-44.45, 25.4) * mm, "radius": 2.73 * mm});
            skCircle(sketch, "E55.MirrorC", {"center": v(44.45, 25.4) * mm, "radius": 2.73 * mm});
            skSolve(sketch);
        }
        {
            var Q0;
            Q0 = qSketchRegion(id + "F20", true);
            extrude(context, id + "F21", {"entities" : qUnion([Q0]), "operationType" : NewBodyOperationType.ADD, "oppositeDirection" : true, "depth" : 3.17 * mm});
        }
        {
            var Q0;
            Q0=makeQuery(id+"F21.boolean.opBoolean","MERGE",FACE,{"derivedFrom":[makeQuery(id+"F1.opExtrude","CAP_FACE",FACE,{"disambiguationData":[OSD([sQuery(id+"F0.wireOp",EDGE,"E1"),sQuery(id+"F0.wireOp",EDGE,"E2"),sQuery(id+"F0.wireOp",EDGE,"E4"),sQuery(id+"F0.wireOp",EDGE,"E5"),sQuery(id+"F0.wireOp",EDGE,"E7.MirrorCS"),sQuery(id+"F0.wireOp",EDGE,"E8.MirrorCS"),sQuery(id+"F0.wireOp",EDGE,"E10.MirrorCS"),sQuery(id+"F0.wireOp",EDGE,"E11.MirrorCS")])],"isStart":false}),makeQuery(id+"F21.opExtrude","CAP_FACE",FACE,{"disambiguationData":[OSD([sQuery(id+"F20.wireOp",EDGE,"E52")])],"isStart":true}),makeQuery(id+"F21.opExtrude","CAP_FACE",FACE,{"disambiguationData":[OSD([sQuery(id+"F20.wireOp",EDGE,"E53.MirrorC")])],"isStart":true}),makeQuery(id+"F21.opExtrude","CAP_FACE",FACE,{"disambiguationData":[OSD([sQuery(id+"F20.wireOp",EDGE,"E54.MirrorC")])],"isStart":true}),makeQuery(id+"F21.opExtrude","CAP_FACE",FACE,{"disambiguationData":[OSD([sQuery(id+"F20.wireOp",EDGE,"E55.MirrorC")])],"isStart":true})]});
            var sketch = newSketch(context, id + "F22", { "sketchPlane" : qUnion([Q0])});
            skCircle(sketch, "E56", {"center": v(-44.45, 25.4) * mm, "radius": 1.59 * mm});
            skCircle(sketch, "E57.MirrorC", {"center": v(44.45, 25.4) * mm, "radius": 1.59 * mm});
            skCircle(sketch, "E58.MirrorC", {"center": v(-44.45, -25.4) * mm, "radius": 1.59 * mm});
            skCircle(sketch, "E59.MirrorC", {"center": v(44.45, -25.4) * mm, "radius": 1.59 * mm});
            skSolve(sketch);
        }
        {
            var Q0;
            Q0 = qSketchRegion(id + "F22", true);
            extrude(context, id + "F23", {"entities" : qUnion([Q0]), "operationType" : NewBodyOperationType.REMOVE, "oppositeDirection" : true, "depth" : 12.7 * mm});
        }
    });
